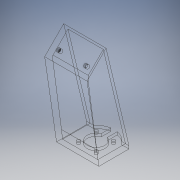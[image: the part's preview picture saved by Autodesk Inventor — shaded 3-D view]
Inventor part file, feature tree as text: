
AUTODESK INVENTOR PART (.ipt)
format: ipt  version: 2016 (Build 200138000, 138)  size: 256,000 bytes
history: native  units: in
note: dims shown in document units (in); Inventor stores cm internally (conversion verified against a paired STEP export)
features: sketch x15, extrude x13, hole x2, chamfer x2
ambient origin geometry x8: Origin, YZ Plane, XZ Plane, XY Plane, X Axis, Y Axis, Z Axis, Center Point
bodies: Solid1 (feature_tree)
feature tree (32):
  extrude  "Extrusion1"  Depth=0.1575in TaperAngle=0.0deg
  extrude  "Extrusion2"  Depth=0.7874in
  extrude  "Extrusion3"  Depth=0.1969in
  extrude  "Extrusion4"  Depth=0.9843in
  hole  "Hole1"  [1 undecoded]
  chamfer  "Chamfer1"  Distance=1.5748in Angle=360.0deg
  extrude  "Extrusion6"  Depth=1.3081in TaperAngle=45.0deg
  extrude  "Extrusion7"  Depth=0.1575in TaperAngle=0.0deg
  extrude  "Extrusion8"  Depth=0.1575in TaperAngle=0.0deg
  hole  "Hole3"  [1 undecoded]
  extrude  "Extrusion9"  Depth=0.3543in
  extrude  "Extrusion10"  Depth=1.0in TaperAngle=0.0deg
  extrude  "Extrusion11"  Depth=1.8898in
  chamfer  "Chamfer2"  Distance=1.0in
  extrude  "Extrusion12"  Depth=0.5in TaperAngle=45.0deg
  extrude  "Extrusion13"  Depth=1.0in TaperAngle=0.0deg
  extrude  "Extrusion14"  Depth=1.0in TaperAngle=0.0deg
  sketch  "Sketch1"  dims[d0=2.0472in d4=0.1575in d5=0.0in]
  sketch  "Sketch2"  dims[d6=2.0472in d7=1.811in d8=0.7874in]
  sketch  "Sketch3"  dims[d10=0.1575in d11=0.0in d12=0.1969in]
  sketch  "Sketch4"  dims[d13=4.5669in d14=0.0in d15=0.9843in]
  sketch  "Sketch5"  dims[d16=0.9843in d17=0.1575in d18=0.0in]
  sketch  "Sketch6"  dims[d19=0.4872in]
  sketch  "Sketch8"  dims[d20=0.4872in d21=1.5748in d23=360.0deg]
  sketch  "Sketch9"  dims[d25=0.164in d26=0.75in d27=0.375in d28=0.25in d29=0.5635in d30=1.0in d31=0.8108in d32=1.3081in d33=0.125in d34=45.0deg]
  sketch  "Sketch10"  dims[d48=1.3in d49=0.0in d50=0.1575in d51=0.0in]
  sketch  "Sketch11"  dims[d52=1.5in d53=0.1575in d54=0.0in]
  sketch  "Sketch12"  dims[d55=2.3622in d56=0.4311in]
  sketch  "Sketch13"  dims[d57=0.4311in]
  sketch  "Sketch14"  dims[d58=0.1969in d59=0.75in d60=0.375in d61=0.25in d62=0.5635in d63=1.0in d64=0.8108in d65=0.3543in]
  sketch  "Sketch15"  dims[d66=0.1772in d67=1.0in d68=0.0in]
  sketch  "Sketch17"  dims[d69=2.3in d70=0.0in d71=1.8898in d72=1.0in d73=0.0in d74=0.5in d75=0.0591in d76=45.0deg d77=1.0in d78=0.0in d81=1.0in d82=0.0in d83=1.0in d84=0.0in]
note: 2 required parameter values undecoded (feature->parameter linkage not recoverable at this tier; creation-order binding heuristic only, values carry confidence <= 0.55)
